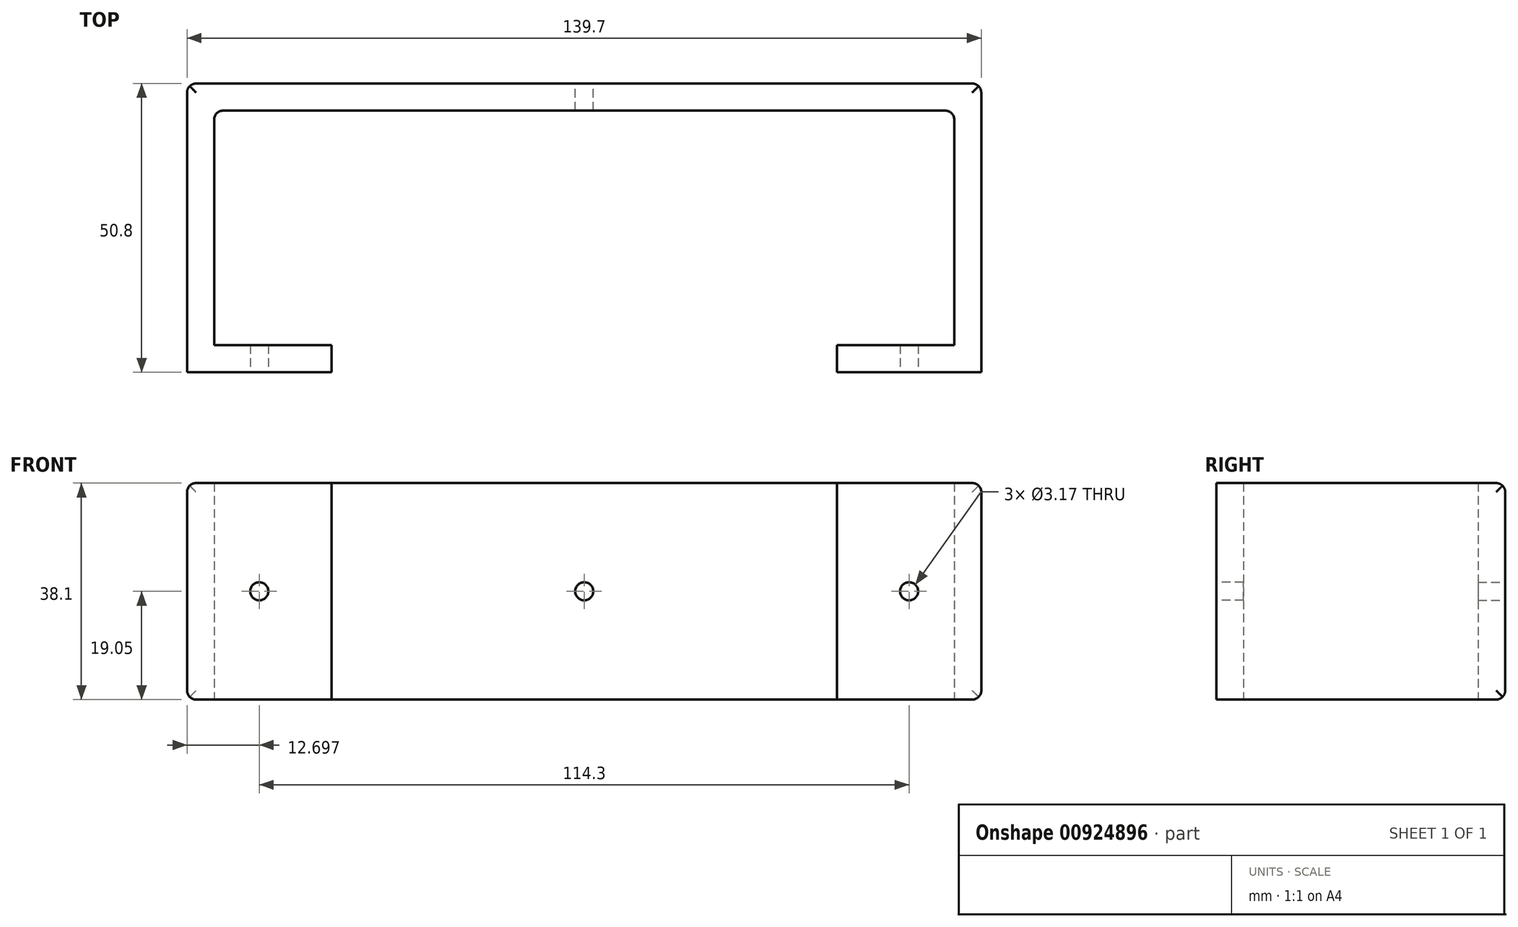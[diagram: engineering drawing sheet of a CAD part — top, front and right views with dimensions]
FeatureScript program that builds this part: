
annotation { "Feature Type Name" : "Feature", "Feature Type Description" : "" }
export const myFeature = defineFeature(function(context is Context, id is Id, definition is map)
    precondition{}
    {
        {
            var Q0;
            Q0=qCreatedBy(makeId("Top.planeOp"),FACE);
            var sketch = newSketch(context, id + "F0", { "sketchPlane" : qUnion([Q0])});
            skLineSegment(sketch, "E0", {"start": v(-44.46, -25.4) * mm, "end": v(-69.86, -25.4) * mm});
            skLineSegment(sketch, "E1", {"start": v(-69.86, -25.4) * mm, "end": v(-69.86, 23.8) * mm});
            skLineSegment(sketch, "E2", {"start": v(-68.26, 25.4) * mm, "end": v(68.24, 25.4) * mm});
            skLineSegment(sketch, "E3", {"start": v(69.84, 23.8) * mm, "end": v(69.84, -25.4) * mm});
            skLineSegment(sketch, "E4", {"start": v(69.84, -25.4) * mm, "end": v(44.44, -25.4) * mm});
            skLineSegment(sketch, "E5", {"start": v(44.44, -25.4) * mm, "end": v(44.44, -20.64) * mm});
            skLineSegment(sketch, "E6", {"start": v(44.44, -20.64) * mm, "end": v(65.07, -20.64) * mm});
            skLineSegment(sketch, "E7", {"start": v(65.07, -20.64) * mm, "end": v(65.07, 19.04) * mm});
            skLineSegment(sketch, "E8", {"start": v(63.47, 20.64) * mm, "end": v(-63.5, 20.64) * mm});
            skLineSegment(sketch, "E9", {"start": v(-65.1, 19.04) * mm, "end": v(-65.1, -20.64) * mm});
            skLineSegment(sketch, "E10", {"start": v(-65.1, -20.64) * mm, "end": v(-44.45, -20.64) * mm});
            skLineSegment(sketch, "E11", {"start": v(-44.45, -20.64) * mm, "end": v(-44.46, -25.4) * mm});
            skPoint(sketch, "E12.visualSharp", {"position": v(-69.86, 25.4) * mm});
            skArc(sketch, "E12.filletArc", {"start": v(-68.26, 25.4) * mm, "mid": v(-69.4, 24.93) * mm, "end": v(-69.86, 23.8) * mm});
            skPoint(sketch, "E13.visualSharp", {"position": v(69.84, 25.4) * mm});
            skArc(sketch, "E13.filletArc", {"start": v(69.84, 23.8) * mm, "mid": v(69.37, 24.93) * mm, "end": v(68.24, 25.4) * mm});
            skPoint(sketch, "E14.visualSharp", {"position": v(-65.1, 20.64) * mm});
            skArc(sketch, "E14.filletArc", {"start": v(-63.5, 20.64) * mm, "mid": v(-64.63, 20.17) * mm, "end": v(-65.1, 19.04) * mm});
            skPoint(sketch, "E15.visualSharp", {"position": v(65.07, 20.64) * mm});
            skArc(sketch, "E15.filletArc", {"start": v(65.07, 19.04) * mm, "mid": v(64.6, 20.17) * mm, "end": v(63.47, 20.64) * mm});
            skSolve(sketch);
        }
        {
            var Q0;
            Q0 = qSketchRegion(id + "F0", true);
            extrude(context, id + "F1", {"entities" : qUnion([Q0]), "depth" : 38.1 * mm, "offsetDistance" : 25.4 * mm});
        }
        {
            var Q0;
            Q0=makeQuery(id+"F1.opExtrude","SWEPT_FACE",FACE,{"disambiguationData":[OSD([sQuery(id+"F0.wireOp",EDGE,"E0")])]});
            var sketch = newSketch(context, id + "F2", { "sketchPlane" : qUnion([Q0])});
            skCircle(sketch, "E16", {"center": v(-57.16, 19.05) * mm, "radius": 1.59 * mm});
            skCircle(sketch, "E17", {"center": v(57.14, 19.05) * mm, "radius": 1.59 * mm});
            skSolve(sketch);
        }
        {
            var Q0;
            Q0 = qSketchRegion(id + "F2", true);
            extrude(context, id + "F3", {"entities" : qUnion([Q0]), "operationType" : NewBodyOperationType.REMOVE, "oppositeDirection" : true, "depth" : 4.76 * mm, "offsetDistance" : 25.4 * mm});
        }
        {
            var Q0;
            Q0=makeQuery(id+"F1.opExtrude","SWEPT_FACE",FACE,{"disambiguationData":[OSD([sQuery(id+"F0.wireOp",EDGE,"E2")])]});
            var sketch = newSketch(context, id + "F4", { "sketchPlane" : qUnion([Q0])});
            skCircle(sketch, "E18", {"center": v(0, 19.05) * mm, "radius": 1.59 * mm});
            skSolve(sketch);
        }
        {
            var Q0;
            Q0 = qSketchRegion(id + "F4", true);
            extrude(context, id + "F5", {"entities" : qUnion([Q0]), "operationType" : NewBodyOperationType.REMOVE, "oppositeDirection" : true, "depth" : 4.76 * mm, "offsetDistance" : 25.4 * mm});
        }
        {
            var Q0;
            Q0=makeQuery(id+"F1.opExtrude","SWEPT_FACE",FACE,{"disambiguationData":[OSD([sQuery(id+"F0.wireOp",EDGE,"E2")])]});
            var sketch = newSketch(context, id + "F6", { "sketchPlane" : qUnion([Q0])});
            skLineSegment(sketch, "E19", {"start": v(-68.24, 38.1) * mm, "end": v(-68.24, 38.1) * mm});
            skLineSegment(sketch, "E20", {"start": v(-69.84, 36.5) * mm, "end": v(-69.84, 36.5) * mm});
            skPoint(sketch, "E21.visualSharp", {"position": v(-69.84, 38.1) * mm});
            skArc(sketch, "E21.filletArc", {"start": v(-68.24, 38.1) * mm, "mid": v(-69.37, 37.63) * mm, "end": v(-69.84, 36.5) * mm});
            skLineSegment(sketch, "E22", {"start": v(-68.24, 0) * mm, "end": v(-68.24, 0) * mm});
            skLineSegment(sketch, "E23", {"start": v(-69.84, 1.6) * mm, "end": v(-69.84, 1.6) * mm});
            skPoint(sketch, "E24.visualSharp", {"position": v(-69.84, 0) * mm});
            skArc(sketch, "E24.filletArc", {"start": v(-69.84, 1.6) * mm, "mid": v(-69.37, 0.47) * mm, "end": v(-68.24, 0) * mm});
            skLineSegment(sketch, "E25", {"start": v(68.26, 0) * mm, "end": v(68.26, 0) * mm});
            skLineSegment(sketch, "E26", {"start": v(69.86, 1.6) * mm, "end": v(69.86, 1.6) * mm});
            skPoint(sketch, "E27.visualSharp", {"position": v(69.86, 0) * mm});
            skArc(sketch, "E27.filletArc", {"start": v(68.26, 0) * mm, "mid": v(69.4, 0.47) * mm, "end": v(69.86, 1.6) * mm});
            skLineSegment(sketch, "E28", {"start": v(68.26, 38.1) * mm, "end": v(68.26, 38.1) * mm});
            skLineSegment(sketch, "E29", {"start": v(69.86, 36.5) * mm, "end": v(69.86, 36.5) * mm});
            skPoint(sketch, "E30.visualSharp", {"position": v(69.86, 38.1) * mm});
            skArc(sketch, "E30.filletArc", {"start": v(69.86, 36.5) * mm, "mid": v(69.4, 37.63) * mm, "end": v(68.26, 38.1) * mm});
            skLineSegment(sketch, "E31", {"start": v(68.26, 38.1) * mm, "end": v(69.86, 38.1) * mm});
            skLineSegment(sketch, "E32", {"start": v(69.86, 38.1) * mm, "end": v(69.86, 36.5) * mm});
            skLineSegment(sketch, "E33", {"start": v(69.86, 1.6) * mm, "end": v(69.86, 0) * mm});
            skLineSegment(sketch, "E34", {"start": v(69.86, 0) * mm, "end": v(68.26, 0) * mm});
            skLineSegment(sketch, "E35", {"start": v(-69.84, 38.1) * mm, "end": v(-69.84, 36.5) * mm});
            skLineSegment(sketch, "E36", {"start": v(-69.84, 38.1) * mm, "end": v(-68.24, 38.1) * mm});
            skLineSegment(sketch, "E37", {"start": v(-69.84, 1.6) * mm, "end": v(-69.84, 0) * mm});
            skLineSegment(sketch, "E38", {"start": v(-68.24, 0) * mm, "end": v(-69.84, 0) * mm});
            skSolve(sketch);
        }
        {
            var Q0;
            Q0 = qSketchRegion(id + "F6", true);
            extrude(context, id + "F7", {"entities" : qUnion([Q0]), "operationType" : NewBodyOperationType.REMOVE, "oppositeDirection" : true, "depth" : 50.8 * mm, "offsetDistance" : 25.4 * mm});
        }
        {
            var Q0;
            Q0=makeQuery(id+"F1.opExtrude","SWEPT_FACE",FACE,{"disambiguationData":[OSD([sQuery(id+"F0.wireOp",EDGE,"E3")])]});
            var sketch = newSketch(context, id + "F8", { "sketchPlane" : qUnion([Q0])});
            skLineSegment(sketch, "E39", {"start": v(23.8, 38.1) * mm, "end": v(23.8, 38.1) * mm});
            skLineSegment(sketch, "E40", {"start": v(25.4, 36.5) * mm, "end": v(25.4, 36.5) * mm});
            skPoint(sketch, "E41.visualSharp", {"position": v(25.4, 38.1) * mm});
            skArc(sketch, "E41.filletArc", {"start": v(25.4, 36.5) * mm, "mid": v(24.93, 37.63) * mm, "end": v(23.8, 38.1) * mm});
            skLineSegment(sketch, "E42", {"start": v(23.8, 0) * mm, "end": v(23.8, 0) * mm});
            skLineSegment(sketch, "E43", {"start": v(25.4, 1.6) * mm, "end": v(25.4, 1.6) * mm});
            skPoint(sketch, "E44.visualSharp", {"position": v(25.4, 0) * mm});
            skArc(sketch, "E44.filletArc", {"start": v(23.8, 0) * mm, "mid": v(24.93, 0.47) * mm, "end": v(25.4, 1.6) * mm});
            skLineSegment(sketch, "E45", {"start": v(25.4, 1.6) * mm, "end": v(25.4, 0) * mm});
            skLineSegment(sketch, "E46", {"start": v(25.4, 0) * mm, "end": v(23.8, 0) * mm});
            skLineSegment(sketch, "E47", {"start": v(23.8, 38.1) * mm, "end": v(25.4, 38.1) * mm});
            skLineSegment(sketch, "E48", {"start": v(25.4, 36.5) * mm, "end": v(25.4, 38.1) * mm});
            skSolve(sketch);
        }
        {
            var Q0;
            Q0 = qSketchRegion(id + "F8", true);
            extrude(context, id + "F9", {"entities" : qUnion([Q0]), "operationType" : NewBodyOperationType.REMOVE, "oppositeDirection" : true, "depth" : 139.7 * mm, "offsetDistance" : 25.4 * mm});
        }
    });
